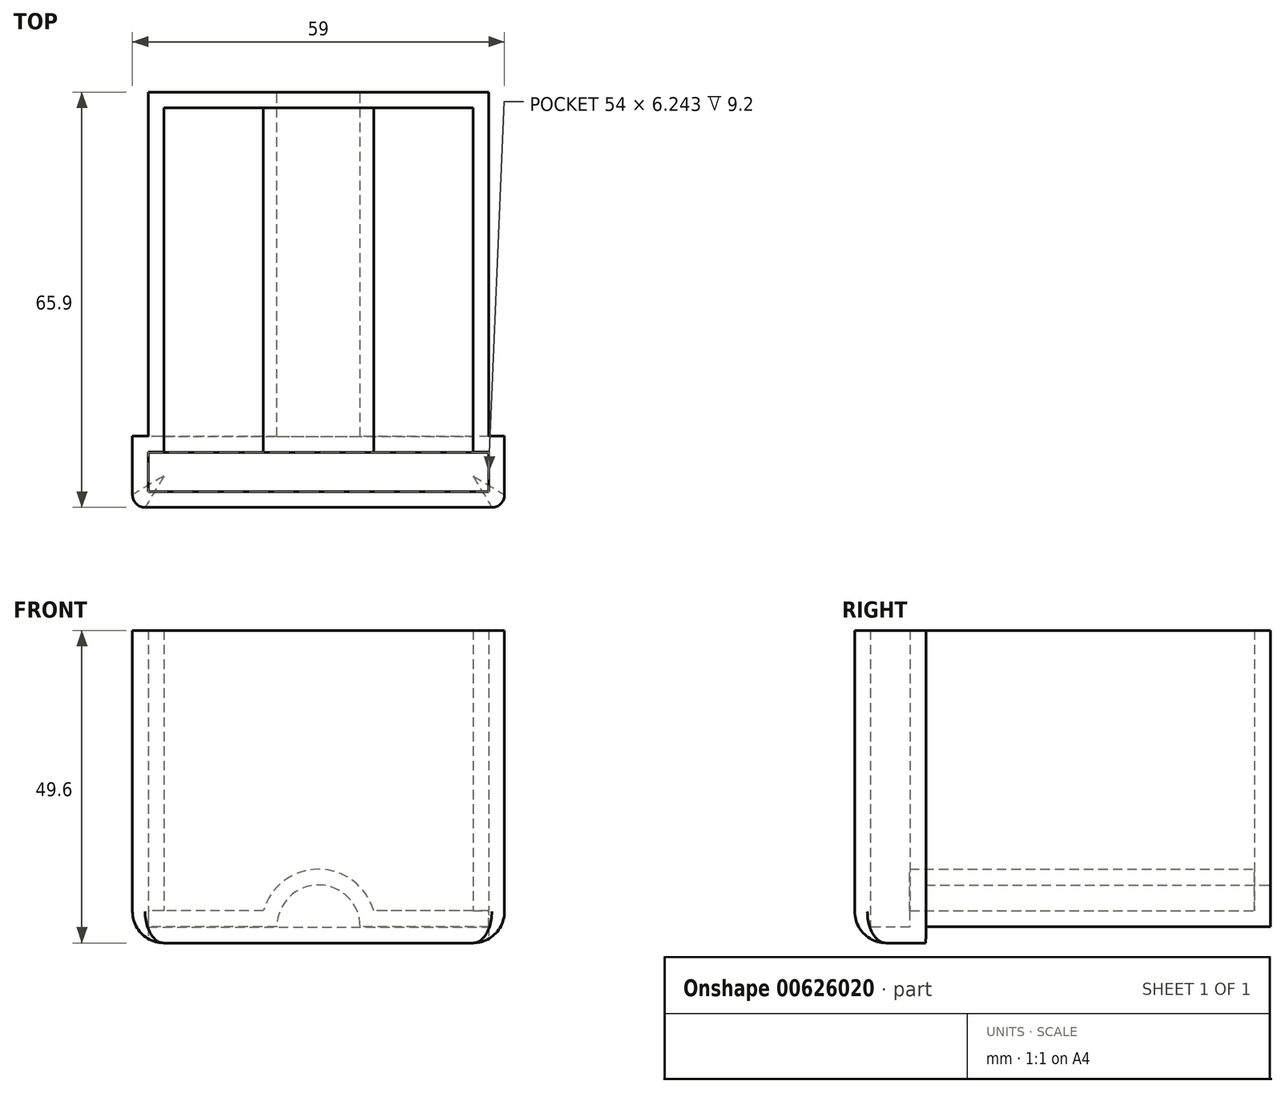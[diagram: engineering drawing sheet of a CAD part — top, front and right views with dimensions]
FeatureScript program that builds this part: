
annotation { "Feature Type Name" : "Feature", "Feature Type Description" : "" }
export const myFeature = defineFeature(function(context is Context, id is Id, definition is map)
    precondition{}
    {
        {
            var Q0;
            Q0=qCreatedBy(makeId("Top.planeOp"),FACE);
            var sketch = newSketch(context, id + "F0", { "sketchPlane" : qUnion([Q0])});
            skLineSegment(sketch, "E0", {"start": v(0, 30.8) * mm, "end": v(27, 30.8) * mm});
            skLineSegment(sketch, "E1", {"start": v(27, 30.8) * mm, "end": v(27, -23.8) * mm});
            skLineSegment(sketch, "E2", {"start": v(27, -23.8) * mm, "end": v(29.5, -23.8) * mm});
            skLineSegment(sketch, "E3", {"start": v(29.5, -23.8) * mm, "end": v(29.5, -35.1) * mm});
            skLineSegment(sketch, "E4", {"start": v(29.5, -35.1) * mm, "end": v(0, -35.1) * mm});
            skLineSegment(sketch, "E5.MirrorCS", {"start": v(0, 30.8) * mm, "end": v(-27, 30.8) * mm});
            skLineSegment(sketch, "E6.MirrorCS", {"start": v(-27, 30.8) * mm, "end": v(-27, -23.8) * mm});
            skLineSegment(sketch, "E7.MirrorCS", {"start": v(-27, -23.8) * mm, "end": v(-29.5, -23.8) * mm});
            skLineSegment(sketch, "E8.MirrorCS", {"start": v(-29.5, -23.8) * mm, "end": v(-29.5, -35.1) * mm});
            skLineSegment(sketch, "E9.MirrorCS", {"start": v(-29.5, -35.1) * mm, "end": v(0, -35.1) * mm});
            skPoint(sketch, "E10", {"position": v(0, 0) * mm});
            skLineSegment(sketch, "E11", {"start": v(-29.5, -35.1) * mm, "end": v(-29.5, 30.8) * mm});
            skSolve(sketch);
        }
        {
            var Q0;
            Q0 = qSketchRegion(id + "F0", true);
            extrude(context, id + "F1", {"entities" : qUnion([Q0]), "depth" : 49.6 * mm, "offsetDistance" : 25 * mm, "symmetric" : true});
        }
        {
            var Q0;
            Q0=makeQuery(id+"F1.opExtrude","SWEPT_FACE",FACE,{"disambiguationData":[OSD([sQuery(id+"F0.wireOp",EDGE,"E0"),sQuery(id+"F0.wireOp",EDGE,"E5.MirrorCS")])]});
            var sketch = newSketch(context, id + "F2", { "sketchPlane" : qUnion([Q0])});
            skLineSegment(sketch, "E12", {"start": v(-27, -22.2) * mm, "end": v(27, -22.2) * mm});
            skSolve(sketch);
        }
        {
            var Q0;
            {var subQ0=sQuery(id+"F2.wireOp",EDGE,"E12");Q0=makeQuery(id+"F2.imprint","IMPRINT",FACE,{"disambiguationData":[TD([[makeQuery(id+"F2.imprint","IMPRINT",EDGE,{"derivedFrom":subQ0}),-1.0]])]});}
            extrude(context, id + "F3", {"entities" : qUnion([Q0]), "operationType" : NewBodyOperationType.REMOVE, "oppositeDirection" : true, "depth" : 54.66 * mm, "offsetDistance" : 25 * mm});
        }
        {
            var Q0;
            Q0=makeQuery(id+"F1.opExtrude","SWEPT_FACE",FACE,{"disambiguationData":[OSD([sQuery(id+"F0.wireOp",EDGE,"E0"),sQuery(id+"F0.wireOp",EDGE,"E5.MirrorCS")])]});
            var sketch = newSketch(context, id + "F4", { "sketchPlane" : qUnion([Q0])});
            skArc(sketch, "E13", {"start": v(6.6, -22.2) * mm, "mid": v(0, -15.6) * mm, "end": v(-6.6, -22.2) * mm});
            skSolve(sketch);
        }
        {
            var Q0;
            Q0 = qSketchRegion(id + "F4", true);
            var Q1;
            {var subQ0=sQuery(id+"F4.wireOp",EDGE,"E13");Q1=makeQuery(id+"F4.imprint","IMPRINT",FACE,{"disambiguationData":[TD([[makeQuery(id+"F4.imprint","IMPRINT",EDGE,{"derivedFrom":subQ0}),1.0]])]});}
            extrude(context, id + "F5", {"entities" : qUnion([Q0, Q1]), "operationType" : NewBodyOperationType.REMOVE, "oppositeDirection" : true, "depth" : 54.66 * mm, "offsetDistance" : 25 * mm});
        }
        {
            var Q0;
            Q0=makeQuery(id+"F1.opExtrude","CAP_FACE",FACE,{"disambiguationData":[OSD([sQuery(id+"F0.wireOp",EDGE,"E0"),sQuery(id+"F0.wireOp",EDGE,"E1"),sQuery(id+"F0.wireOp",EDGE,"E2"),sQuery(id+"F0.wireOp",EDGE,"E3"),sQuery(id+"F0.wireOp",EDGE,"E4"),sQuery(id+"F0.wireOp",EDGE,"E5.MirrorCS"),sQuery(id+"F0.wireOp",EDGE,"E6.MirrorCS"),sQuery(id+"F0.wireOp",EDGE,"E7.MirrorCS"),sQuery(id+"F0.wireOp",EDGE,"E8.MirrorCS"),sQuery(id+"F0.wireOp",EDGE,"E9.MirrorCS")])],"isStart":false});
            shell(context, id + "F6", {"entities" : qUnion([Q0]), "thickness" : 2.5 * mm});
        }
        {
            var Q0;
            Q0=makeQuery(id+"F1.opExtrude","SWEPT_EDGE",EDGE,{"disambiguationData":[OSD([sQuery(id+"F0.wireOp",EDGE,"E9.MirrorCS"),sQuery(id+"F0.wireOp",EDGE,"E11")])]});
            fillet(context, id + "F7", {"entities" : qUnion([Q0]), "radius" : 2 * mm, "tangentPropagation" : true, "allowEdgeOverflow" : false});
        }
        {
            var Q0;
            Q0=makeQuery(id+"F1.opExtrude","SWEPT_EDGE",EDGE,{"disambiguationData":[OSD([sQuery(id+"F0.wireOp",EDGE,"E3"),sQuery(id+"F0.wireOp",EDGE,"E4")])]});
            fillet(context, id + "F8", {"entities" : qUnion([Q0]), "radius" : 2 * mm, "tangentPropagation" : true, "allowEdgeOverflow" : false});
        }
        {
            var Q0;
            Q0=makeQuery(id+"F1.opExtrude","CAP_EDGE",EDGE,{"disambiguationData":[OSD([sQuery(id+"F0.wireOp",EDGE,"E3")])],"isStart":true});
            fillet(context, id + "F9", {"entities" : qUnion([Q0]), "radius" : 5 * mm, "tangentPropagation" : true, "allowEdgeOverflow" : false});
        }
    });
